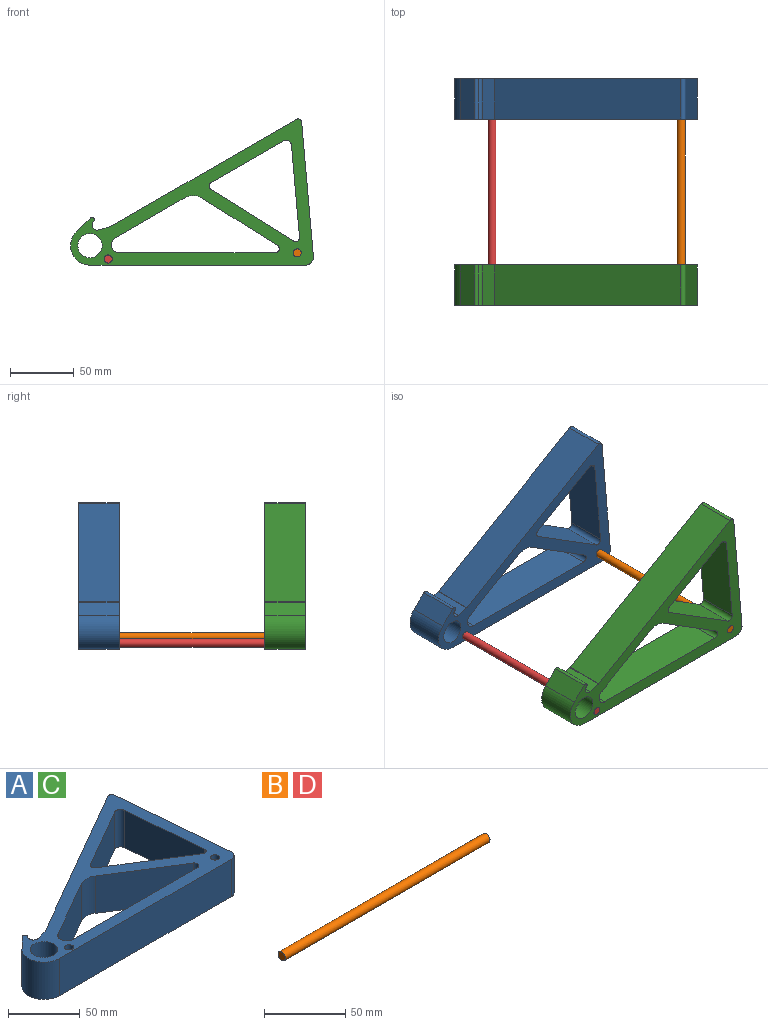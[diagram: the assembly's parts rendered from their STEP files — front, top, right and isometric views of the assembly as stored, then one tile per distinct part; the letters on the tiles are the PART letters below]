
ASSEMBLY  parts=4 mates=3
PART A: 28 faces, bbox 190.5x114.7x31.8 mm
  f0: cylinder r=6.35mm len=31.75mm, axis (0,0,-1), area 527.8mm2, adj f1,f16,f20,f21
  f1: plane 54.59x31.75mm, normal (0.5,-0.87,0), area 2001.2mm2, adj f0,f20,f21,f25
  f2: plane 59.33x37.17mm, normal (-0.53,-0.85,0), area 2222.9mm2, adj f20,f21,f24,f25
  f3: cylinder r=1.27mm len=31.75mm, axis (0,0,-1), area 10.5mm2, adj f4,f17,f20,f21
  f4: plane 31.75x9.36mm, normal (-0.26,0.97,0), area 307.7mm2, adj f3,f5,f20,f21
  f5: cylinder r=3.94mm len=31.75mm, axis (0,0,-1), area 328.1mm2, adj f4,f6,f20,f21
  f6: cylinder r=1.91mm len=31.75mm, axis (0,0,-1), area 190mm2, adj f5,f7,f20,f21
  f7: plane 31.75x10.89mm, normal (-0.71,0.71,0), area 488.5mm2, adj f6,f8,f20,f21
  f8: cylinder r=15.24mm len=31.75mm, axis (0,0,-1), area 1140.7mm2, adj f7,f9,f20,f21
  f9: plane 168.93x31.75mm, normal (0,-1,0), area 5363.7mm2, adj f8,f10,f20,f21
  f10: cylinder r=6.35mm len=31.75mm, axis (0,0,-1), area 334.3mm2, adj f9,f11,f20,f21
  f11: plane 105.22x31.75mm, normal (1,0.09,0), area 3353.6mm2, adj f10,f12,f20,f21
  f12: cylinder r=2.79mm len=31.75mm, axis (0,0,-1), area 177.8mm2, adj f11,f17,f20,f21
  f13: cylinder r=4.24mm len=31.75mm, axis (0,0,-1), area 270.3mm2, adj f14,f18,f20,f21
  f14: plane 72.21x31.75mm, normal (-1,-0.09,0), area 2301.3mm2, adj f13,f20,f21,f22
  f15: plane 64.4x40.34mm, normal (0.53,0.85,0), area 2412.7mm2, adj f20,f21,f22,f23
  f16: plane 122.12x31.75mm, normal (0,1,0), area 3877.3mm2, adj f0,f20,f21,f24
  f17: plane 145.59x84.05mm, normal (-0.5,0.87,0), area 5337.4mm2, adj f3,f12,f20,f21
  f18: plane 56.56x32.66mm, normal (0.5,-0.87,0), area 2073.6mm2, adj f13,f20,f21,f23
  f19: cylinder r=9.53mm len=31.75mm, axis (0,0,-1), area 1900.2mm2, adj f20,f21
  f20: plane 190.52x114.67mm, normal (0,0,1), area 5517mm2, adj f0,f1,f2,f3,f4,f5,f6,f7
  f21: plane 190.52x114.67mm, normal (0,0,-1), area 5517mm2, adj f0,f1,f2,f3,f4,f5,f6,f7
  f22: cylinder r=3.23mm len=31.75mm, axis (0,0,1), area 227.1mm2, adj f14,f15,f20,f21
  f23: cylinder r=3.23mm len=31.75mm, axis (0,0,-1), area 210.8mm2, adj f15,f18,f20,f21
  f24: cylinder r=3.23mm len=31.75mm, axis (0,0,-1), area 264.4mm2, adj f2,f16,f20,f21
  f25: cylinder r=12.7mm len=31.75mm, axis (0,0,1), area 436.8mm2, adj f1,f2,f20,f21
  f26: cylinder r=3.17mm len=31.75mm, axis (0,0,1), area 633.4mm2, adj f20,f21
  f27: cylinder r=3.17mm len=31.75mm, axis (0,0,1), area 633.4mm2, adj f20,f21
PART B: 3 faces, bbox 177.8x6.4x6.4 mm
  f0: cylinder r=3.17mm len=177.8mm, axis (-1,0,0), area 3547mm2, adj f1,f2
  f1: plane 6.35x6.35mm, normal (1,0,0), area 31.7mm2, adj f0
  f2: plane 6.35x6.35mm, normal (-1,0,0), area 31.7mm2, adj f0
PART C: same geometry as A
PART D: same geometry as B
PLACE A rot(axis=(1,0,0),90deg) t=(7.9,15.88,25.4)mm
PLACE B rot(axis=(0.58,-0.58,-0.58),120deg) t=(165.73,15.88,9.52)mm
PLACE C rot(axis=(1,0,0),90deg) t=(7.9,-130.18,25.4)mm
PLACE D rot(axis=(-0.58,0.58,-0.58),120deg) t=(11.08,15.88,4.76)mm
MATE fastened C.f26 <-> B.f0  axis (0,-1,0) through (162.56,-161.93,9.52)mm
MATE fastened B.f0 <-> A.f26  axis (0,1,0) through (162.56,15.88,9.52)mm
MATE fastened D.f0 <-> A.f27  axis (0,1,0) through (14.25,15.88,4.76)mm
